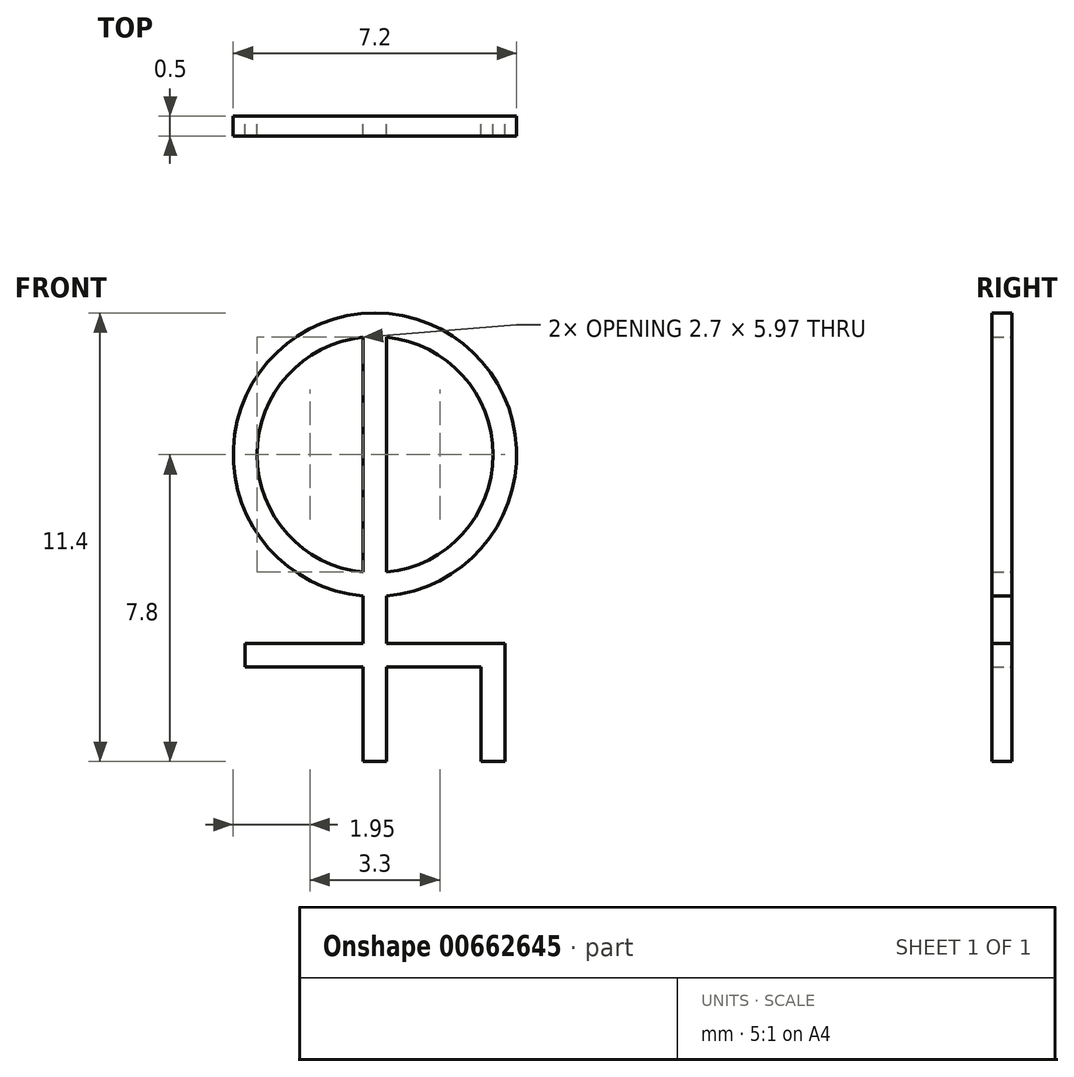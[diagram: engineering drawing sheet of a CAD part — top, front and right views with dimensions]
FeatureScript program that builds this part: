
annotation { "Feature Type Name" : "Feature", "Feature Type Description" : "" }
export const myFeature = defineFeature(function(context is Context, id is Id, definition is map)
    precondition{}
    {
        {
            var Q0;
            Q0=qCreatedBy(makeId("Front.planeOp"),FACE);
            var sketch = newSketch(context, id + "F0", { "sketchPlane" : qUnion([Q0])});
            skArc(sketch, "E0", {"start": v(0.3, -2.98) * mm, "mid": v(3, 0) * mm, "end": v(0.3, 2.98) * mm});
            skArc(sketch, "E1.0", {"start": v(0.3, -3.59) * mm, "mid": v(0, 3.6) * mm, "end": v(-0.3, -3.59) * mm});
            skLineSegment(sketch, "E2", {"start": v(-0.3, 2.98) * mm, "end": v(-0.3, -2.98) * mm});
            skLineSegment(sketch, "E3", {"start": v(0.3, 2.98) * mm, "end": v(0.3, -2.98) * mm});
            skLineSegment(sketch, "E4", {"start": v(0.3, -7.8) * mm, "end": v(-0.3, -7.8) * mm});
            skLineSegment(sketch, "E5", {"start": v(-3.3, -4.8) * mm, "end": v(-0.3, -4.8) * mm});
            skLineSegment(sketch, "E6", {"start": v(3.3, -4.8) * mm, "end": v(3.3, -7.8) * mm});
            skLineSegment(sketch, "E7", {"start": v(3.3, -7.8) * mm, "end": v(2.7, -7.8) * mm});
            skLineSegment(sketch, "E8", {"start": v(2.7, -7.8) * mm, "end": v(2.7, -5.4) * mm});
            skLineSegment(sketch, "E9", {"start": v(2.7, -5.4) * mm, "end": v(0.3, -5.4) * mm});
            skLineSegment(sketch, "E10", {"start": v(-3.3, -4.8) * mm, "end": v(-3.3, -5.4) * mm});
            skArc(sketch, "E11.trimOffspring", {"start": v(-0.3, 2.98) * mm, "mid": v(-3, 0) * mm, "end": v(-0.3, -2.98) * mm});
            skLineSegment(sketch, "E12.trimOffspring", {"start": v(-0.3, -3.59) * mm, "end": v(-0.3, -4.8) * mm});
            skLineSegment(sketch, "E13.trimOffspring", {"start": v(0.3, -3.59) * mm, "end": v(0.3, -4.8) * mm});
            skLineSegment(sketch, "E14.trimOffspring", {"start": v(-0.3, -5.4) * mm, "end": v(-0.3, -7.8) * mm});
            skLineSegment(sketch, "E15.trimOffspring", {"start": v(0.3, -4.8) * mm, "end": v(3.3, -4.8) * mm});
            skLineSegment(sketch, "E16.trimOffspring", {"start": v(0.3, -5.4) * mm, "end": v(0.3, -7.8) * mm});
            skLineSegment(sketch, "E17.trimOffspring", {"start": v(-0.3, -5.4) * mm, "end": v(-3.3, -5.4) * mm});
            skSolve(sketch);
        }
        {
            var Q0;
            Q0=makeQuery(id+"F0.imprint","IMPRINT",FACE,{"disambiguationData":[TD([[makeQuery(id+"F0.imprint","IMPRINT",EDGE,{"derivedFrom":sQuery(id+"F0.wireOp",EDGE,"E0")}),-1.0]])]});
            extrude(context, id + "F1", {"entities" : qUnion([Q0]), "depth" : .5 * mm, "offsetDistance" : 25 * mm});
        }
    });
